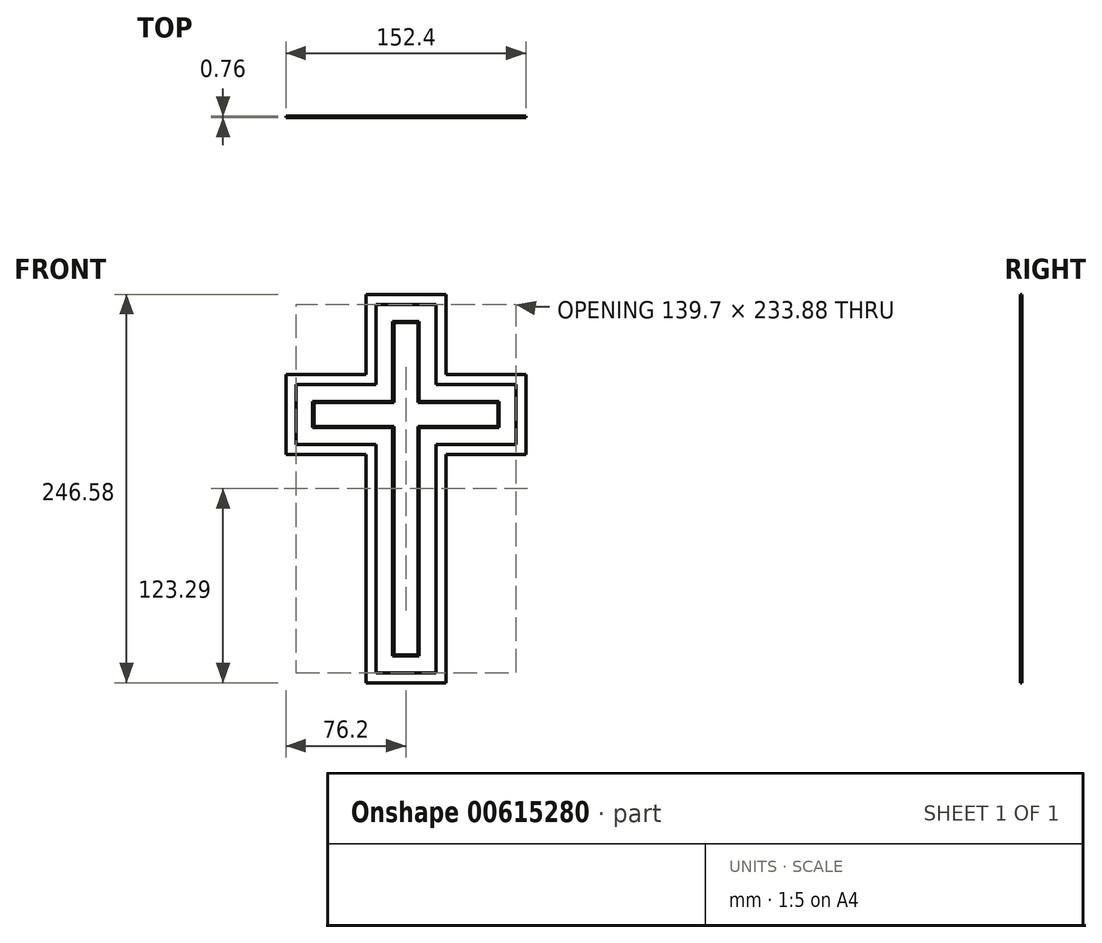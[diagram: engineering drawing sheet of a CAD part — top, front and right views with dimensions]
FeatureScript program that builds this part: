
annotation { "Feature Type Name" : "Feature", "Feature Type Description" : "" }
export const myFeature = defineFeature(function(context is Context, id is Id, definition is map)
    precondition{}
    {
        {
            assignVariable(context, id + "F0", {"name" : "Thickness", "anyValue" : 3 / 4});
        }
        {
            var Q0;
            Q0=qCreatedBy(makeId("Front.planeOp"),FACE);
            var sketch = newSketch(context, id + "F1", { "sketchPlane" : qUnion([Q0])});
            skLineSegment(sketch, "E0.bottom", {"start": v(-76.2, 123.3) * mm, "end": v(76.2, 123.3) * mm, "construction": true});
            skLineSegment(sketch, "E0.top", {"start": v(-76.2, -123.3) * mm, "end": v(76.2, -123.3) * mm, "construction": true});
            skLineSegment(sketch, "E0.left", {"start": v(-76.2, 123.3) * mm, "end": v(-76.2, -123.3) * mm, "construction": true});
            skLineSegment(sketch, "E0.right", {"start": v(76.2, 123.3) * mm, "end": v(76.2, -123.3) * mm, "construction": true});
            skLineSegment(sketch, "E1", {"start": v(-76.2, 123.3) * mm, "end": v(76.2, -123.3) * mm, "construction": true});
            skSolve(sketch);
        }
        {
            var Q0;
            Q0=qCreatedBy(makeId("Front.planeOp"),FACE);
            var sketch = newSketch(context, id + "F2", { "sketchPlane" : qUnion([Q0])});
            skLineSegment(sketch, "E2.bottom", {"start": v(-25.4, 123.3) * mm, "end": v(25.4, 123.3) * mm});
            skLineSegment(sketch, "E2.top", {"start": v(-25.4, -123.3) * mm, "end": v(25.4, -123.3) * mm});
            skLineSegment(sketch, "E2.left", {"start": v(-25.4, 123.3) * mm, "end": v(-25.4, -123.3) * mm});
            skLineSegment(sketch, "E2.right", {"start": v(25.4, 123.3) * mm, "end": v(25.4, -123.3) * mm});
            skLineSegment(sketch, "E3", {"start": v(25.4, 123.3) * mm, "end": v(-25.4, -123.3) * mm, "construction": true});
            skSolve(sketch);
        }
        {
            var Q0;
            Q0=qCreatedBy(makeId("Front.planeOp"),FACE);
            var sketch = newSketch(context, id + "F3", { "sketchPlane" : qUnion([Q0])});
            skLineSegment(sketch, "E4.bottom", {"start": v(-76.2, 72.5) * mm, "end": v(76.2, 72.5) * mm});
            skLineSegment(sketch, "E4.top", {"start": v(-76.2, 21.7) * mm, "end": v(76.2, 21.7) * mm});
            skLineSegment(sketch, "E4.left", {"start": v(-76.2, 72.5) * mm, "end": v(-76.2, 21.7) * mm});
            skLineSegment(sketch, "E4.right", {"start": v(76.2, 72.5) * mm, "end": v(76.2, 21.7) * mm});
            skPoint(sketch, "E5", {"position": v(-76.2, 47.1) * mm});
            skSolve(sketch);
        }
        {
            var Q0;
            Q0 = qSketchRegion(id + "F2", true);
            extrude(context, id + "F4", {"entities" : qUnion([Q0]), "endBound" : BoundingType.SYMMETRIC, "depth" : (getVariable(context, 'Thickness')) * mm, "offsetDistance" : 25.4 * mm});
        }
        {
            var Q0;
            Q0 = qSketchRegion(id + "F3", true);
            extrude(context, id + "F5", {"entities" : qUnion([Q0]), "operationType" : NewBodyOperationType.ADD, "endBound" : BoundingType.SYMMETRIC, "depth" : (getVariable(context, 'Thickness')) * mm, "offsetDistance" : 25.4 * mm});
        }
        {
            var Q0;
            Q0=makeQuery(id+"F5.boolean.opBoolean","MERGE",FACE,{"derivedFrom":[makeQuery(id+"F4.opExtrude","CAP_FACE",FACE,{"disambiguationData":[OSD([sQuery(id+"F2.wireOp",EDGE,"E2.bottom"),sQuery(id+"F2.wireOp",EDGE,"E2.top"),sQuery(id+"F2.wireOp",EDGE,"E2.left"),sQuery(id+"F2.wireOp",EDGE,"E2.right")])],"isStart":false}),makeQuery(id+"F5.opExtrude","CAP_FACE",FACE,{"disambiguationData":[OSD([sQuery(id+"F3.wireOp",EDGE,"E4.bottom"),sQuery(id+"F3.wireOp",EDGE,"E4.top"),sQuery(id+"F3.wireOp",EDGE,"E4.left"),sQuery(id+"F3.wireOp",EDGE,"E4.right")])],"isStart":false})]});
            var sketch = newSketch(context, id + "F6", { "sketchPlane" : qUnion([Q0])});
            skLineSegment(sketch, "E6.0", {"start": v(-69.85, 66.14) * mm, "end": v(-69.85, 28.04) * mm});
            skLineSegment(sketch, "E6.1", {"start": v(19.05, 66.14) * mm, "end": v(69.85, 66.14) * mm});
            skLineSegment(sketch, "E6.2", {"start": v(19.05, 116.94) * mm, "end": v(19.05, 66.14) * mm});
            skLineSegment(sketch, "E6.3", {"start": v(-19.05, 116.94) * mm, "end": v(19.05, 116.94) * mm});
            skLineSegment(sketch, "E6.4", {"start": v(-19.05, 116.94) * mm, "end": v(-19.05, 66.14) * mm});
            skLineSegment(sketch, "E6.5", {"start": v(69.85, 66.14) * mm, "end": v(69.85, 28.04) * mm});
            skLineSegment(sketch, "E6.6", {"start": v(-69.85, 66.14) * mm, "end": v(-19.05, 66.14) * mm});
            skLineSegment(sketch, "E6.7", {"start": v(19.05, 28.04) * mm, "end": v(69.85, 28.04) * mm});
            skLineSegment(sketch, "E6.8", {"start": v(19.05, 28.04) * mm, "end": v(19.05, -116.94) * mm});
            skLineSegment(sketch, "E6.9", {"start": v(-19.05, -116.94) * mm, "end": v(19.05, -116.94) * mm});
            skLineSegment(sketch, "E6.10", {"start": v(-19.05, 28.04) * mm, "end": v(-19.05, -116.94) * mm});
            skLineSegment(sketch, "E6.11", {"start": v(-69.85, 28.04) * mm, "end": v(-19.05, 28.04) * mm});
            skLineSegment(sketch, "E7.0", {"start": v(-12.7, 110.6) * mm, "end": v(12.7, 110.6) * mm});
            skLineSegment(sketch, "E7.1", {"start": v(-12.7, 34.4) * mm, "end": v(-12.7, -110.6) * mm});
            skLineSegment(sketch, "E7.2", {"start": v(-63.5, 34.4) * mm, "end": v(-12.7, 34.4) * mm});
            skLineSegment(sketch, "E7.3", {"start": v(-63.5, 59.8) * mm, "end": v(-63.5, 34.4) * mm});
            skLineSegment(sketch, "E7.4", {"start": v(-63.5, 59.8) * mm, "end": v(-12.7, 59.8) * mm});
            skLineSegment(sketch, "E7.5", {"start": v(-12.7, -110.6) * mm, "end": v(12.7, -110.6) * mm});
            skLineSegment(sketch, "E7.6", {"start": v(-12.7, 110.6) * mm, "end": v(-12.7, 59.8) * mm});
            skLineSegment(sketch, "E7.7", {"start": v(12.7, 34.4) * mm, "end": v(12.7, -110.6) * mm});
            skLineSegment(sketch, "E7.8", {"start": v(12.7, 34.4) * mm, "end": v(63.5, 34.4) * mm});
            skLineSegment(sketch, "E7.9", {"start": v(63.5, 59.8) * mm, "end": v(63.5, 34.4) * mm});
            skLineSegment(sketch, "E7.10", {"start": v(12.7, 59.8) * mm, "end": v(63.5, 59.8) * mm});
            skLineSegment(sketch, "E7.11", {"start": v(12.7, 110.6) * mm, "end": v(12.7, 59.8) * mm});
            skSolve(sketch);
        }
        {
            var Q0;
            Q0 = qSketchRegion(id + "F6", true);
            extrude(context, id + "F7", {"entities" : qUnion([Q0]), "operationType" : NewBodyOperationType.REMOVE, "oppositeDirection" : true, "depth" : 3.17 * mm, "offsetDistance" : 25.4 * mm});
        }
        {
            var Q0;
            Q0=makeQuery(id+"F5.boolean.opBoolean","MERGE",FACE,{"derivedFrom":[makeQuery(id+"F4.opExtrude","CAP_FACE",FACE,{"disambiguationData":[OSD([sQuery(id+"F2.wireOp",EDGE,"E2.bottom"),sQuery(id+"F2.wireOp",EDGE,"E2.top"),sQuery(id+"F2.wireOp",EDGE,"E2.left"),sQuery(id+"F2.wireOp",EDGE,"E2.right")])],"isStart":false}),makeQuery(id+"F5.opExtrude","CAP_FACE",FACE,{"disambiguationData":[OSD([sQuery(id+"F3.wireOp",EDGE,"E4.bottom"),sQuery(id+"F3.wireOp",EDGE,"E4.top"),sQuery(id+"F3.wireOp",EDGE,"E4.left"),sQuery(id+"F3.wireOp",EDGE,"E4.right")])],"isStart":false})]});
            chamfer(context, id + "F8", {"entities" : qUnion([Q0]), "width" : 5.08 * mm, "tangentPropagation" : true});
        }
    });
